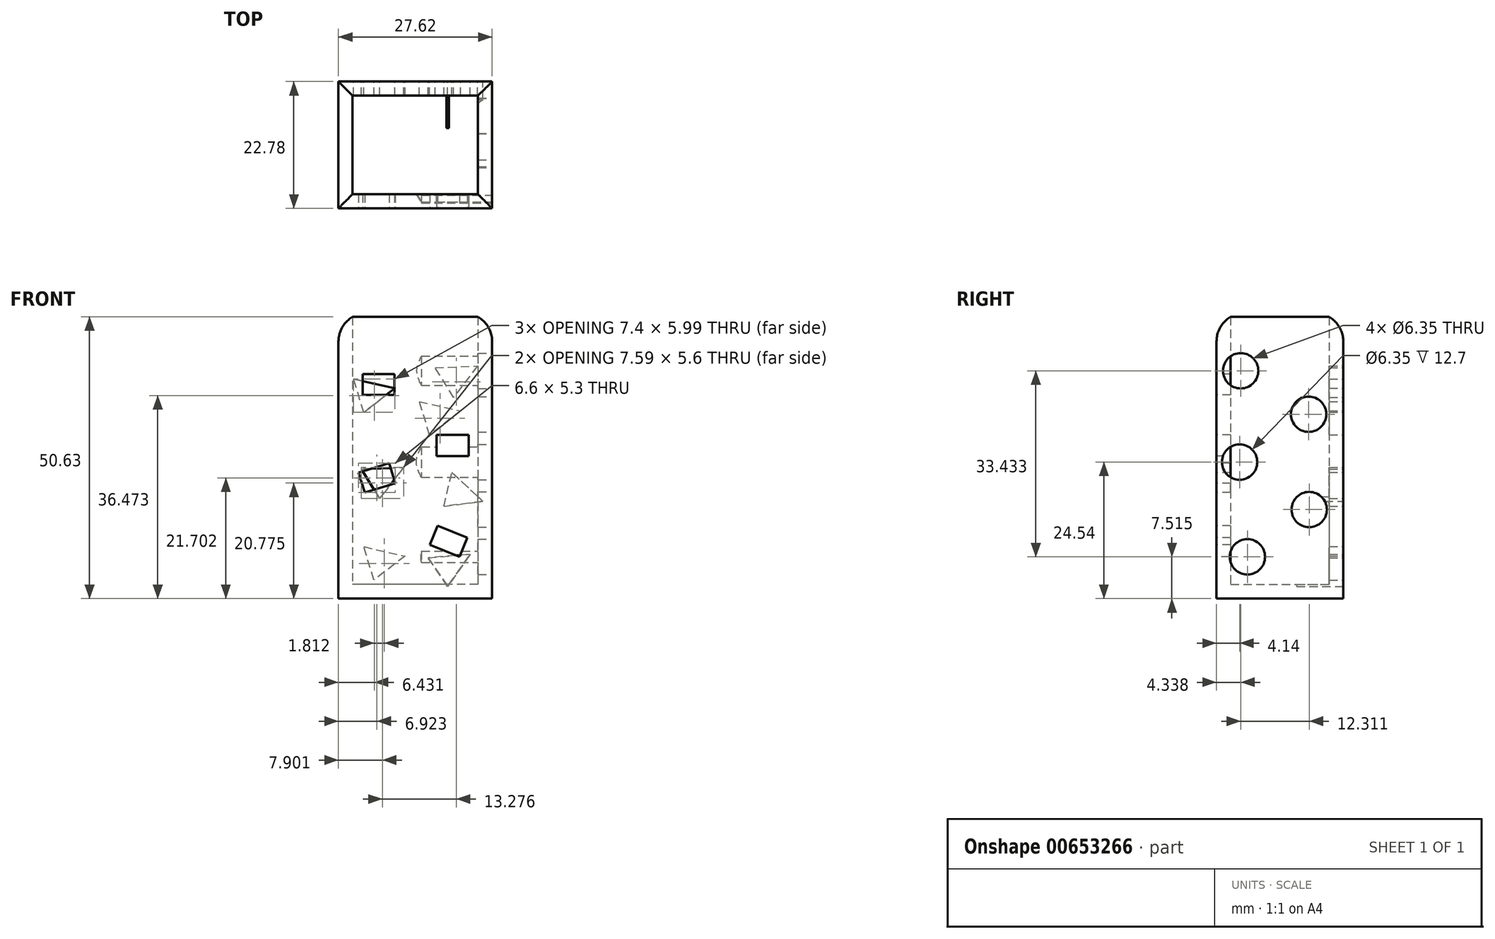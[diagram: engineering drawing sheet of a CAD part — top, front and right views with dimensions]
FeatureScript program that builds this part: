
annotation { "Feature Type Name" : "Feature", "Feature Type Description" : "" }
export const myFeature = defineFeature(function(context is Context, id is Id, definition is map)
    precondition{}
    {
        {
            var Q0;
            Q0=qCreatedBy(makeId("Top.planeOp"),FACE);
            var sketch = newSketch(context, id + "F0", { "sketchPlane" : qUnion([Q0])});
            skLineSegment(sketch, "E0.bottom", {"start": v(0, 0) * mm, "end": v(-27.62, 0) * mm});
            skLineSegment(sketch, "E0.top", {"start": v(0, 22.78) * mm, "end": v(-27.62, 22.78) * mm});
            skLineSegment(sketch, "E0.left", {"start": v(0, 0) * mm, "end": v(0, 22.78) * mm});
            skLineSegment(sketch, "E0.right", {"start": v(-27.62, 0) * mm, "end": v(-27.62, 22.78) * mm});
            skSolve(sketch);
        }
        {
            var Q0;
            Q0 = qSketchRegion(id + "F0", true);
            extrude(context, id + "F1", {"entities" : qUnion([Q0]), "depth" : 51.3 * mm, "offsetDistance" : 25.4 * mm});
        }
        {
            var Q0;
            Q0=makeQuery(id+"F1.opExtrude","CAP_FACE",FACE,{"disambiguationData":[OSD([sQuery(id+"F0.wireOp",EDGE,"E0.bottom"),sQuery(id+"F0.wireOp",EDGE,"E0.top"),sQuery(id+"F0.wireOp",EDGE,"E0.left"),sQuery(id+"F0.wireOp",EDGE,"E0.right")])],"isStart":false});
            shell(context, id + "F2", {"entities" : qUnion([Q0]), "thickness" : 2.54 * mm});
        }
        {
            var Q0;
            Q0=makeQuery(id+"F1.opExtrude","CAP_EDGE",EDGE,{"disambiguationData":[OSD([sQuery(id+"F0.wireOp",EDGE,"E0.bottom")])],"isStart":false});
            var Q1;
            Q1=makeQuery(id+"F1.opExtrude","CAP_EDGE",EDGE,{"disambiguationData":[OSD([sQuery(id+"F0.wireOp",EDGE,"E0.right")])],"isStart":false});
            var Q2;
            Q2=makeQuery(id+"F1.opExtrude","CAP_EDGE",EDGE,{"disambiguationData":[OSD([sQuery(id+"F0.wireOp",EDGE,"E0.top")])],"isStart":false});
            var Q3;
            Q3=makeQuery(id+"F1.opExtrude","CAP_EDGE",EDGE,{"disambiguationData":[OSD([sQuery(id+"F0.wireOp",EDGE,"E0.left")])],"isStart":false});
            fillet(context, id + "F3", {"entities" : qUnion([Q0, Q1, Q2, Q3]), "radius" : 5.08 * mm, "tangentPropagation" : true, "allowEdgeOverflow" : false});
        }
        {
            var Q0;
            Q0=makeQuery(id+"F1.opExtrude","SWEPT_FACE",FACE,{"disambiguationData":[OSD([sQuery(id+"F0.wireOp",EDGE,"E0.bottom")])]});
            var sketch = newSketch(context, id + "F4", { "sketchPlane" : qUnion([Q0])});
            skLineSegment(sketch, "E1.bottom", {"start": v(-23.29, 40.33) * mm, "end": v(-17.54, 40.33) * mm});
            skLineSegment(sketch, "E1.top", {"start": v(-23.29, 36.57) * mm, "end": v(-17.54, 36.57) * mm});
            skLineSegment(sketch, "E1.left", {"start": v(-23.29, 40.33) * mm, "end": v(-23.29, 36.57) * mm});
            skLineSegment(sketch, "E1.right", {"start": v(-17.54, 40.33) * mm, "end": v(-17.54, 36.57) * mm});
            skLineSegment(sketch, "E2.bottom", {"start": v(-9.97, 29.4) * mm, "end": v(-4.22, 29.4) * mm});
            skLineSegment(sketch, "E2.top", {"start": v(-9.97, 25.64) * mm, "end": v(-4.22, 25.64) * mm});
            skLineSegment(sketch, "E2.left", {"start": v(-9.97, 29.4) * mm, "end": v(-9.97, 25.64) * mm});
            skLineSegment(sketch, "E2.right", {"start": v(-4.22, 29.4) * mm, "end": v(-4.22, 25.64) * mm});
            skLineSegment(sketch, "E3.bottom", {"start": v(-24, 22.64) * mm, "end": v(-18.51, 24.35) * mm});
            skLineSegment(sketch, "E3.top", {"start": v(-22.88, 19.05) * mm, "end": v(-17.4, 20.76) * mm});
            skLineSegment(sketch, "E3.left", {"start": v(-24, 22.64) * mm, "end": v(-22.88, 19.05) * mm});
            skLineSegment(sketch, "E3.right", {"start": v(-18.51, 24.35) * mm, "end": v(-17.4, 20.76) * mm});
            skLineSegment(sketch, "E4.bottom", {"start": v(-9.78, 13.14) * mm, "end": v(-4.46, 10.97) * mm});
            skLineSegment(sketch, "E4.top", {"start": v(-11.2, 9.65) * mm, "end": v(-5.88, 7.5) * mm});
            skLineSegment(sketch, "E4.left", {"start": v(-9.78, 13.14) * mm, "end": v(-11.2, 9.65) * mm});
            skLineSegment(sketch, "E4.right", {"start": v(-4.46, 10.97) * mm, "end": v(-5.88, 7.5) * mm});
            skSolve(sketch);
        }
        {
            var Q0;
            Q0 = qSketchRegion(id + "F4", true);
            extrude(context, id + "F5", {"entities" : qUnion([Q0]), "operationType" : NewBodyOperationType.REMOVE, "oppositeDirection" : true, "depth" : 4.83 * mm, "offsetDistance" : 25.4 * mm});
        }
        {
            var Q0;
            Q0=makeQuery(id+"F1.opExtrude","SWEPT_FACE",FACE,{"disambiguationData":[OSD([sQuery(id+"F0.wireOp",EDGE,"E0.left")])]});
            var sketch = newSketch(context, id + "F6", { "sketchPlane" : qUnion([Q0])});
            skCircle(sketch, "E5", {"center": v(4.34, 40.95) * mm, "radius": 3.49 * mm});
            skCircle(sketch, "E6", {"center": v(16.55, 33.14) * mm, "radius": 3.49 * mm});
            skCircle(sketch, "E7", {"center": v(4.14, 24.54) * mm, "radius": 3.49 * mm});
            skCircle(sketch, "E8", {"center": v(16.65, 16) * mm, "radius": 3.49 * mm});
            skCircle(sketch, "E9", {"center": v(5.54, 7.51) * mm, "radius": 3.49 * mm});
            skSolve(sketch);
        }
        {
            var Q0;
            Q0=sQuery(id+"F6.wireOp",VERTEX,"E5.center");
            var Q1;
            Q1=sQuery(id+"F6.wireOp",VERTEX,"E6.center");
            var Q2;
            Q2=sQuery(id+"F6.wireOp",VERTEX,"E7.center");
            var Q3;
            Q3=sQuery(id+"F6.wireOp",VERTEX,"E8.center");
            var Q4;
            Q4=sQuery(id+"F6.wireOp",VERTEX,"E9.center");
            var Q5;
            Q5=makeQuery(id+"F1.opExtrude","SWEPT_BODY",BODY,{"disambiguationData":[OSD([sQuery(id+"F0.wireOp",EDGE,"E0.bottom"),sQuery(id+"F0.wireOp",EDGE,"E0.top"),sQuery(id+"F0.wireOp",EDGE,"E0.left"),sQuery(id+"F0.wireOp",EDGE,"E0.right")])]});
            hole(context, id + "F7", {"style" : HoleStyle.SIMPLE, "endStyle" : HoleEndStyle.BLIND, "holeDiameter" : 6.35 * mm, "majorDiameter" : 6.35 * mm, "holeDepth" : 12.7 * mm, "isTappedThrough" : true, "tappedDepth" : 12.7 * mm, "tapClearance" : 3, "locations" : qUnion([Q0, Q1, Q2, Q3, Q4]), "scope" : qUnion([Q5])});
        }
        {
            var Q0;
            Q0=makeQuery(id+"F1.opExtrude","SWEPT_FACE",FACE,{"disambiguationData":[OSD([sQuery(id+"F0.wireOp",EDGE,"E0.top")])]});
            var sketch = newSketch(context, id + "F8", { "sketchPlane" : qUnion([Q0])});
            skLineSegment(sketch, "E10", {"start": v(5.67, 33.72) * mm, "end": v(11.26, 29.42) * mm});
            skLineSegment(sketch, "E11", {"start": v(11.26, 29.42) * mm, "end": v(13.08, 35.4) * mm});
            skLineSegment(sketch, "E12", {"start": v(13.08, 35.4) * mm, "end": v(5.67, 33.72) * mm});
            skLineSegment(sketch, "E13", {"start": v(15.92, 23.58) * mm, "end": v(20.2, 17.97) * mm});
            skLineSegment(sketch, "E14", {"start": v(20.2, 17.97) * mm, "end": v(23.51, 23.3) * mm});
            skLineSegment(sketch, "E15", {"start": v(23.51, 23.3) * mm, "end": v(15.92, 23.58) * mm});
            skLineSegment(sketch, "E16", {"start": v(1.68, 17.5) * mm, "end": v(8.67, 16.57) * mm});
            skLineSegment(sketch, "E17", {"start": v(8.67, 16.57) * mm, "end": v(7.25, 22.67) * mm});
            skLineSegment(sketch, "E18", {"start": v(7.25, 22.67) * mm, "end": v(1.68, 17.5) * mm});
            skLineSegment(sketch, "E19", {"start": v(15.67, 7.64) * mm, "end": v(21.26, 3.34) * mm});
            skLineSegment(sketch, "E20", {"start": v(21.26, 3.34) * mm, "end": v(23.08, 9.33) * mm});
            skLineSegment(sketch, "E21", {"start": v(23.08, 9.33) * mm, "end": v(15.67, 7.64) * mm});
            skLineSegment(sketch, "E22", {"start": v(3.95, 7.96) * mm, "end": v(8, 2.19) * mm});
            skLineSegment(sketch, "E23", {"start": v(8, 2.19) * mm, "end": v(11.52, 7.36) * mm});
            skLineSegment(sketch, "E24", {"start": v(11.52, 7.36) * mm, "end": v(3.95, 7.96) * mm});
            skLineSegment(sketch, "E25", {"start": v(17.49, 37.78) * mm, "end": v(23.07, 33.48) * mm});
            skLineSegment(sketch, "E26", {"start": v(23.07, 33.48) * mm, "end": v(24.9, 39.47) * mm});
            skLineSegment(sketch, "E27", {"start": v(24.9, 39.47) * mm, "end": v(17.49, 37.78) * mm});
            skLineSegment(sketch, "E28", {"start": v(2.65, 41.78) * mm, "end": v(6.93, 36.18) * mm});
            skLineSegment(sketch, "E29", {"start": v(6.93, 36.18) * mm, "end": v(10.24, 41.5) * mm});
            skLineSegment(sketch, "E30", {"start": v(10.24, 41.5) * mm, "end": v(2.65, 41.78) * mm});
            skSolve(sketch);
        }
        {
            var Q0;
            Q0 = qSketchRegion(id + "F8", true);
            extrude(context, id + "F9", {"entities" : qUnion([Q0]), "operationType" : NewBodyOperationType.REMOVE, "oppositeDirection" : true, "depth" : 8.38 * mm, "offsetDistance" : 25.4 * mm});
        }
    });
